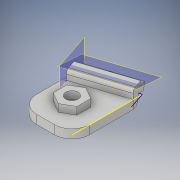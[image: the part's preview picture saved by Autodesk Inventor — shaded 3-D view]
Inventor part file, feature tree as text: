
AUTODESK INVENTOR PART (.ipt)
format: ipt  version: 2018 (Build 220112000, 112)  size: 189,952 bytes
history: native  units: in
note: dims shown in document units (in); Inventor stores cm internally (conversion verified against a paired STEP export)
features: extrude x6, sketch x6, plane x2, fillet x2
ambient origin geometry x8: Origin, YZ Plane, XZ Plane, XY Plane, X Axis, Y Axis, Z Axis, Center Point
bodies: Solid1 (feature_tree)
feature tree (16):
  extrude  "Extrusion1"  Depth=1.1811in
  sketch  "Sketch2"  dims[d2=0.3937in d3=0.1969in d4=0.0in]
  plane  "Work Plane2"
  extrude  "Extrusion2"  Depth=0.1969in TaperAngle=0.0deg
  plane  "Work Plane4"
  extrude  "Extrusion4"  Depth=0.1969in
  extrude  "Extrusion5"  Depth=0.0787in
  extrude  "Extrusion6"  Depth=1.1811in TaperAngle=0.0deg
  fillet  "Fillet2"  Radius=0.1181in
  extrude  "Extrusion7"  [1 undecoded]
  fillet  "Fillet3"  Radius=0.0197in
  sketch  "Sketch1"  dims[d0=1.1811in d1=1.1811in]
  sketch  "Sketch3"  dims[d5=0.1969in d6=0.1969in]
  sketch  "Sketch5"  dims[d7=0.0787in d9=1.0994in]
  sketch  "Sketch7"  dims[d12=0.1378in d13=1.1811in d14=0.0in d20=0.1181in]
  sketch  "Sketch8"  dims[d21=0.1772in d23=-0.1772in d24=0.0197in d25=0.5906in d26=0.0984in d27=0.1181in d28=0.3937in d29=0.0in d31=0.1673in d32=0.0in d34=0.1374in d35=0.1969in d36=1.5748in d37=0.0in d38=0.0in d39=0.0197in d40=0.7874in d41=0.0in d42=0.3937in d43=0.5315in d44=0.2756in]
note: 1 required parameter value undecoded (feature->parameter linkage not recoverable at this tier; creation-order binding heuristic only, values carry confidence <= 0.55)
